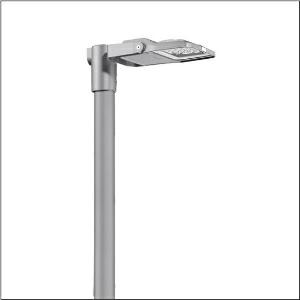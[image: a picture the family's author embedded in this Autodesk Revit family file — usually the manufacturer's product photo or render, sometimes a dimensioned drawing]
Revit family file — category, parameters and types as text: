
# Revit family: floodlight_fl_21_iq_micro___pl33t_5xa7762a2f3a_98d7
name_source: partatom
category: Lighting Fixtures
units: mm (PartAtom-declared; Revit-internal decimal feet)

## family parameters
Cut with Voids When Loaded = No
Host = Face
Light Source = No
Part Type = Normal
Room Calculation Point = No
Round Connector Dimension = Use Diameter
Shared = No

## types (1)
- --- (1 x LED, 2930 lm, 23.1 W, 3000K)
    Apparent Load = 23 VA
    CIE Flux Codes = 26 75 99 100 100
    Color Rendering = 70
    Color Temperature = 3000K
    Default Elevation = 1800 mm
    Description = Floodlight FL 21 iQ micro, floodlight, primary light control with lens, of PMMA, primary optical cover: protective disc, of toughened safety glass, transparent, light distribution: PL33T, light emission: direct distribution, installation type: surface-mounted, lamps: LED, High Power LED, rated values: 2.930lm | 23,1W | 126,8lm/W (begin service life); end service life: 2.930lm | 23,8W; at 50% lumin. flux: 1.465lm | 11W | 133,2lm/W, colour temperature: 3000K, colour rendering: CRI > 70, light colour: 730, light setting 1 begin service life: 100% | 2.930lm | 23,1W | 126,8lm/W | 3.000K, light setting 1 end service life: 23,8W, further light settings possible, control: Auto-Match, Temp-Guard, Night-Set, Smart-Wire, Desk-Remote (wireless, voltage-free reading and setting of iQ features in the workshop via application-optimized NFC function/RFID function), optimised constant luminous flux control (CLO 2.0), Street-Remote, pre-setting: linear dimming characteristic, with terminal, 6-pole, mains connection: 220..240V, AC, 50/60Hz, luminaire housing, of diecast aluminium, powder-coated, SITECO metallic grey (DB 702S), corrosivity category C5 mid according to DIN EN ISO 12944suitable for swimming poolschlorine-resistant, sealing non-destructively replaceable, please order mast flange separately, mast bracket, of steel, galvanised, powder-coated, SITECO metallic grey (DB 702S), protection rating (complete): IP66, insulation class (complete): insulation class II (safety insulation), certification: CE, ENEC, VDE, protection symbol: D, impact resistance: IK07, permissible operating ambient temperature: -40..+40°C, permissible operating ambient temperature for outdoor applications: -40..+50°C, standard: DIN EN 12944, LABS conformity tested according to VDMA 24364:2018-05, packaging unit: 1 piece

Light Distribution: PL33T
    Height = 65 mm
    Lamp = 1 x LED
    Lamp Light Flux = 2930 lm
    Lamp Power = 23.1 W
    Lamp count = 1
    Length = 312 mm
    Luminous efficacy = 127 lm/W
    Manufacturer = Siteco
    ModVariant = No
    Model = 5XA7762A2F3A
    Mounting Place = Pole
    Mounting Type = Pole annexe
    Number of Poles = 1
    OnlyDefault = Yes
    Power Factor = 1
    Product Name = Floodlight FL 21 iQ micro | PL33T
    Product group = floodlight | pylon annexe
    ProductGroupID = 6201
    Protection Class = Protection class II
    Protection Degree = IP 66
    RLX_Detail_Level = 1
    RLX_Emergency_Light_Flux = 0 lm
    RLX_Emergency_Type = 0
    RLX_Emergency_Type_DB = No
    RlxData = <blob elided: 101857 chars, md5=6fded65b>
    Socket = socket
    Standby Power = 0 W
    System Light Flux = 2930 lm
    System Power = 23 W
    Type Comments = factory setting: luminous flux: 100 % | dim-lin: 254 | 455 mA
    Type Image = l_1007121.jpg
    URL = http://relux.com
    VarID = @adj_149017
    Voltage = 0 V
    Weight = 0.00 kg
    Width = 230 mm

## geometry (parser evidence)
native form markers: Blend x4, Sweep x10
no freeform markers — native parametric forms only
